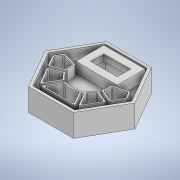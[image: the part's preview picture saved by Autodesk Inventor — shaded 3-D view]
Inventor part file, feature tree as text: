
AUTODESK INVENTOR PART (.ipt)
format: ipt  version: 2022 (Build 260153000, 153)  size: 357,376 bytes
history: native  units: mm
features: sketch x3, extrude x2, shell x1
ambient origin geometry x8: Origin, YZ Plane, XZ Plane, XY Plane, X Axis, Y Axis, Z Axis, Center Point
bodies: Body1 (feature_tree)
feature tree (6):
  shell  "Vaciado1"  Thickness=30.0mm
  extrude  "Extrusión4"  Depth=60.0mm
  sketch  "Boceto5"  dims[d75=6.0mm d92=60.0mm d104=80.0mm]
  extrude  "Extrusión27"  Depth=24.0mm TaperAngle=0.0deg
  sketch  "Boceto8"  dims[d147=20.0mm d148=0.0mm d230=24.0mm d231=0.0mm]
  sketch  "Boceto21"  dims[d232=3.0mm d233=6.0mm d236=3.0mm d237=0.0mm d251=24.0mm d252=0.0mm d253=24.0mm d254=0.0mm d258=2.0mm d260=28.0mm d261=0.0mm d268=6.0mm d269=0.0mm d35=0.5mm d36=0.872665mm d37=0.5mm d38=0.872665mm d70=0.5mm d71=0.872665mm d93=0.5mm d94=0.872665mm d95=0.5mm d96=0.872665mm d99=0.5mm d100=0.872665mm d101=0.5mm d102=0.872665mm d149=0.5mm d150=0.872665mm d151=0.872665mm d152=0.5mm d153=0.872665mm d178=0.5mm d179=0.872665mm d180=0.5mm d181=0.872665mm d250=0.5mm]
